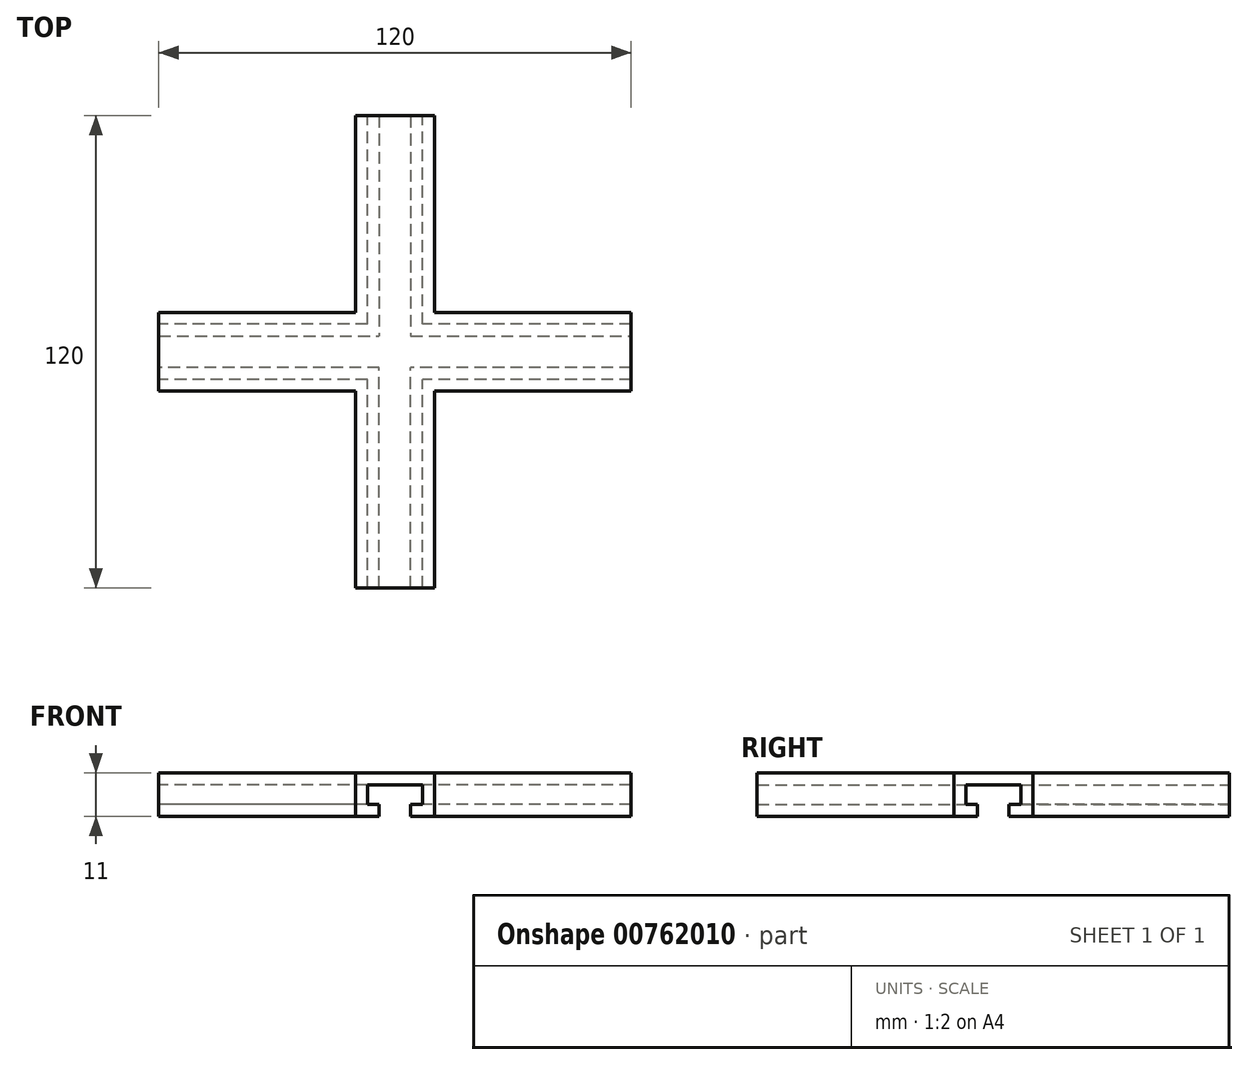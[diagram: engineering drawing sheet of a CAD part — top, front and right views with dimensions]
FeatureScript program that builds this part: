
annotation { "Feature Type Name" : "Feature", "Feature Type Description" : "" }
export const myFeature = defineFeature(function(context is Context, id is Id, definition is map)
    precondition{}
    {
        {
            var Q0;
            Q0=qCreatedBy(makeId("Top.planeOp"),FACE);
            var sketch = newSketch(context, id + "F0", { "sketchPlane" : qUnion([Q0])});
            skLineSegment(sketch, "E0.bottom", {"start": v(10, -60) * mm, "end": v(-10, -60) * mm});
            skLineSegment(sketch, "E0.top", {"start": v(10, 60) * mm, "end": v(-10, 60) * mm});
            skLineSegment(sketch, "E0.left", {"start": v(10, -60) * mm, "end": v(10, -10) * mm});
            skLineSegment(sketch, "E0.right", {"start": v(-10, -60) * mm, "end": v(-10, -10) * mm});
            skPoint(sketch, "E0.middle", {"position": v(0, 0) * mm});
            skLineSegment(sketch, "E1.bottom", {"start": v(60, -10) * mm, "end": v(10, -10) * mm});
            skLineSegment(sketch, "E1.top", {"start": v(60, 10) * mm, "end": v(10, 10) * mm});
            skLineSegment(sketch, "E1.left", {"start": v(60, -10) * mm, "end": v(60, 10) * mm});
            skLineSegment(sketch, "E1.right", {"start": v(-60, -10) * mm, "end": v(-60, 10) * mm});
            skLineSegment(sketch, "E2.trimOffspring", {"start": v(-10, 10) * mm, "end": v(-60, 10) * mm});
            skLineSegment(sketch, "E3.trimOffspring", {"start": v(-10, 10) * mm, "end": v(-10, 60) * mm});
            skLineSegment(sketch, "E4.trimOffspring", {"start": v(-10, -10) * mm, "end": v(-60, -10) * mm});
            skLineSegment(sketch, "E5.trimOffspring", {"start": v(10, 10) * mm, "end": v(10, 60) * mm});
            skLineSegment(sketch, "E6.1", {"start": v(-7, 7) * mm, "end": v(-60, 7) * mm});
            skLineSegment(sketch, "E6.2", {"start": v(-7, 7) * mm, "end": v(-7, 60) * mm});
            skLineSegment(sketch, "E6.4", {"start": v(7, 7) * mm, "end": v(7, 60) * mm});
            skLineSegment(sketch, "E6.6", {"start": v(60, 7) * mm, "end": v(7, 7) * mm});
            skLineSegment(sketch, "E6.7", {"start": v(-7, -7) * mm, "end": v(-60, -7) * mm});
            skLineSegment(sketch, "E6.8", {"start": v(-7, -60) * mm, "end": v(-7, -7) * mm});
            skLineSegment(sketch, "E6.10", {"start": v(7, -60) * mm, "end": v(7, -7) * mm});
            skLineSegment(sketch, "E6.11", {"start": v(60, -7) * mm, "end": v(7, -7) * mm});
            skSolve(sketch);
        }
        {
            var Q0;
            Q0 = qSketchRegion(id + "F0", true);
            extrude(context, id + "F1", {"entities" : qUnion([Q0]), "depth" : 3 * mm, "offsetDistance" : 25 * mm});
        }
        {
            var Q0;
            {var subQ1=sQuery(id+"F0.wireOp",EDGE,"E1.top");Q0=makeQuery(id+"F0.imprint","IMPRINT",FACE,{"disambiguationData":[TD([[makeQuery(id+"F0.imprint","IMPRINT",EDGE,{"derivedFrom":subQ1}),1.0]])]});}
            var Q1;
            {var subQ1=sQuery(id+"F0.wireOp",EDGE,"E2.trimOffspring");Q1=makeQuery(id+"F0.imprint","IMPRINT",FACE,{"disambiguationData":[TD([[makeQuery(id+"F0.imprint","IMPRINT",EDGE,{"derivedFrom":subQ1}),1.0]])]});}
            var Q2;
            {var subQ1=sQuery(id+"F0.wireOp",EDGE,"E0.right");Q2=makeQuery(id+"F0.imprint","IMPRINT",FACE,{"disambiguationData":[TD([[makeQuery(id+"F0.imprint","IMPRINT",EDGE,{"derivedFrom":subQ1}),-1.0]])]});}
            var Q3;
            {var subQ1=sQuery(id+"F0.wireOp",EDGE,"E0.left");Q3=makeQuery(id+"F0.imprint","IMPRINT",FACE,{"disambiguationData":[TD([[makeQuery(id+"F0.imprint","IMPRINT",EDGE,{"derivedFrom":subQ1}),1.0]])]});}
            extrude(context, id + "F2", {"entities" : qUnion([Q0, Q1, Q2, Q3]), "operationType" : NewBodyOperationType.ADD, "oppositeDirection" : true, "depth" : 5 * mm, "offsetDistance" : 25 * mm});
        }
        {
            var Q0;
            Q0=makeQuery(id+"F2.opExtrude","CAP_FACE",FACE,{"disambiguationData":[OSD([sQuery(id+"F0.wireOp",EDGE,"E0.bottom"),sQuery(id+"F0.wireOp",EDGE,"E0.right"),sQuery(id+"F0.wireOp",EDGE,"E1.right"),sQuery(id+"F0.wireOp",EDGE,"E4.trimOffspring"),sQuery(id+"F0.wireOp",EDGE,"E6.7"),sQuery(id+"F0.wireOp",EDGE,"E6.8")])],"isStart":false});
            var sketch = newSketch(context, id + "F3", { "sketchPlane" : qUnion([Q0])});
            skLineSegment(sketch, "E7", {"start": v(-10, 60) * mm, "end": v(-10, 10) * mm});
            skLineSegment(sketch, "E8", {"start": v(-10, 10) * mm, "end": v(-60, 10) * mm});
            skLineSegment(sketch, "E9.0", {"start": v(-4, 60) * mm, "end": v(-4, 10) * mm});
            skLineSegment(sketch, "E10.0", {"start": v(-10, 4) * mm, "end": v(-60, 4) * mm});
            skLineSegment(sketch, "E11", {"start": v(-10, 60) * mm, "end": v(-4, 60) * mm});
            skLineSegment(sketch, "E12", {"start": v(-60, 10) * mm, "end": v(-60, 4) * mm});
            skLineSegment(sketch, "E13", {"start": v(-4, 10) * mm, "end": v(-4, 4) * mm});
            skLineSegment(sketch, "E14", {"start": v(-10, 4) * mm, "end": v(-4, 4) * mm});
            skLineSegment(sketch, "E15.MirrorCS", {"start": v(10, 60) * mm, "end": v(4, 60) * mm});
            skLineSegment(sketch, "E16.MirrorCS", {"start": v(60, 10) * mm, "end": v(60, 4) * mm});
            skLineSegment(sketch, "E17.MirrorCS", {"start": v(4, 10) * mm, "end": v(4, 4) * mm});
            skLineSegment(sketch, "E18.MirrorCS", {"start": v(10, 4) * mm, "end": v(4, 4) * mm});
            skLineSegment(sketch, "E19.MirrorCS", {"start": v(4, 60) * mm, "end": v(4, 10) * mm});
            skLineSegment(sketch, "E20.MirrorCS", {"start": v(10, 4) * mm, "end": v(60, 4) * mm});
            skLineSegment(sketch, "E21.MirrorCS", {"start": v(10, 10) * mm, "end": v(60, 10) * mm});
            skLineSegment(sketch, "E22.MirrorCS", {"start": v(10, 60) * mm, "end": v(10, 10) * mm});
            skLineSegment(sketch, "E23.MirrorCS", {"start": v(10, -4) * mm, "end": v(4, -4) * mm});
            skLineSegment(sketch, "E24.MirrorCS", {"start": v(10, -60) * mm, "end": v(4, -60) * mm});
            skLineSegment(sketch, "E25.MirrorCS", {"start": v(60, -10) * mm, "end": v(60, -4) * mm});
            skLineSegment(sketch, "E26.MirrorCS", {"start": v(4, -10) * mm, "end": v(4, -4) * mm});
            skLineSegment(sketch, "E27.MirrorCS", {"start": v(-10, -60) * mm, "end": v(-4, -60) * mm});
            skLineSegment(sketch, "E28.MirrorCS", {"start": v(-60, -10) * mm, "end": v(-60, -4) * mm});
            skLineSegment(sketch, "E29.MirrorCS", {"start": v(-10, -4) * mm, "end": v(-4, -4) * mm});
            skLineSegment(sketch, "E30.MirrorCS", {"start": v(-4, -10) * mm, "end": v(-4, -4) * mm});
            skLineSegment(sketch, "E31.MirrorCS", {"start": v(10, -4) * mm, "end": v(60, -4) * mm});
            skLineSegment(sketch, "E32.MirrorCS", {"start": v(10, -10) * mm, "end": v(60, -10) * mm});
            skLineSegment(sketch, "E33.MirrorCS", {"start": v(10, -60) * mm, "end": v(10, -10) * mm});
            skLineSegment(sketch, "E34.MirrorCS", {"start": v(4, -60) * mm, "end": v(4, -10) * mm});
            skLineSegment(sketch, "E35.MirrorCS", {"start": v(-10, -60) * mm, "end": v(-10, -10) * mm});
            skLineSegment(sketch, "E36.MirrorCS", {"start": v(-10, -10) * mm, "end": v(-60, -10) * mm});
            skLineSegment(sketch, "E37.MirrorCS", {"start": v(-4, -60) * mm, "end": v(-4, -10) * mm});
            skLineSegment(sketch, "E38.MirrorCS", {"start": v(-10, -4) * mm, "end": v(-60, -4) * mm});
            skSolve(sketch);
        }
        {
            var Q0;
            Q0 = qSketchRegion(id + "F3", true);
            extrude(context, id + "F4", {"entities" : qUnion([Q0]), "operationType" : NewBodyOperationType.ADD, "depth" : 3 * mm, "offsetDistance" : 25 * mm});
        }
    });
